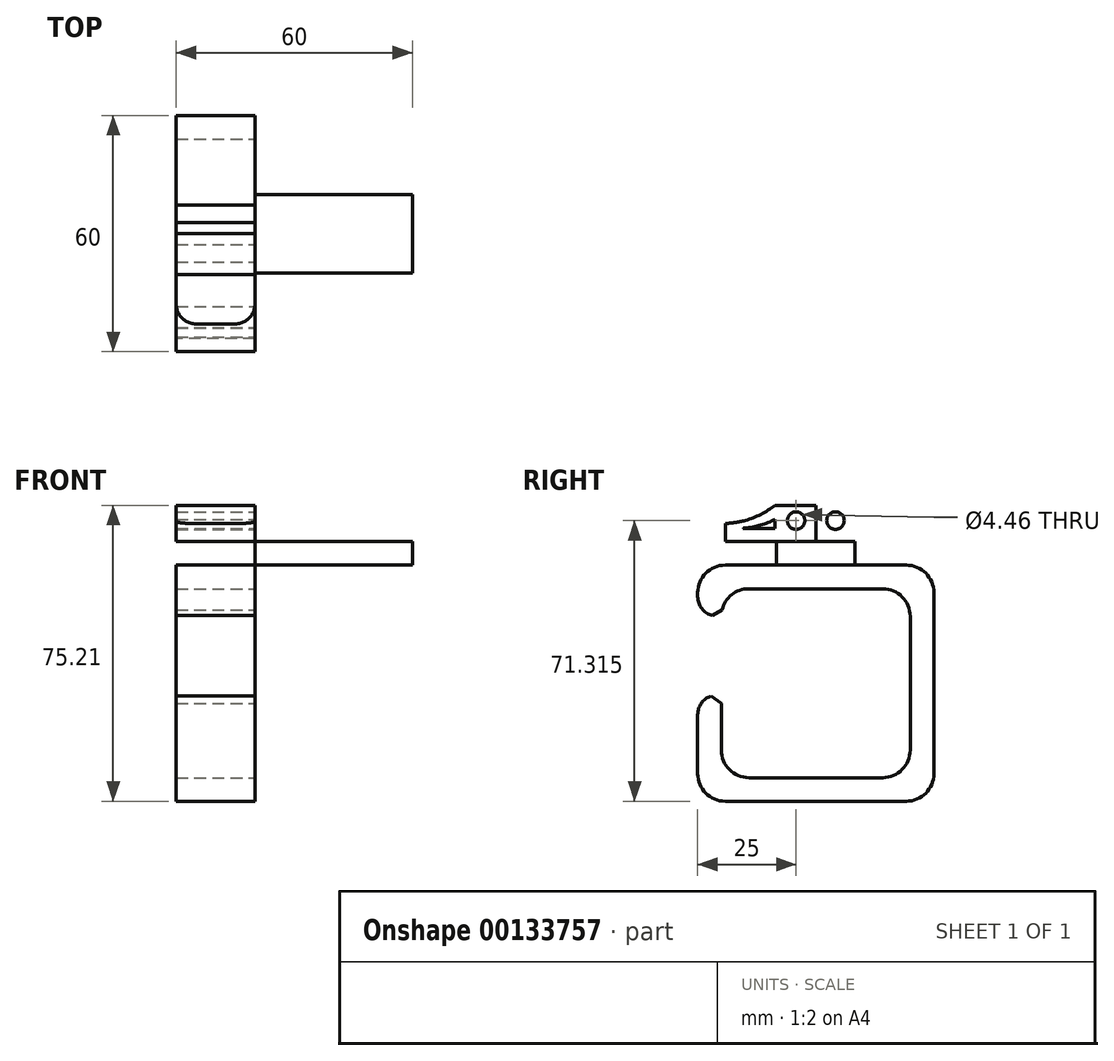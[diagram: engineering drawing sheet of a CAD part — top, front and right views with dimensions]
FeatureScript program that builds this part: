
annotation { "Feature Type Name" : "Feature", "Feature Type Description" : "" }
export const myFeature = defineFeature(function(context is Context, id is Id, definition is map)
    precondition{}
    {
        {
            var Q0;
            Q0=qCreatedBy(makeId("Right.planeOp"),FACE);
            var sketch = newSketch(context, id + "F0", { "sketchPlane" : qUnion([Q0])});
            skLineSegment(sketch, "E0", {"start": v(0, 0) * mm, "end": v(48.5, 0) * mm});
            skLineSegment(sketch, "E1", {"start": v(48.5, 0) * mm, "end": v(48.5, 25) * mm});
            skLineSegment(sketch, "E2", {"start": v(48.5, 25) * mm, "end": v(-71.5, 25) * mm});
            skLineSegment(sketch, "E3", {"start": v(-71.5, 25) * mm, "end": v(-71.5, 0) * mm});
            skLineSegment(sketch, "E4", {"start": v(-71.5, 0) * mm, "end": v(-23, 0) * mm});
            skLineSegment(sketch, "E5", {"start": v(-40, 0) * mm, "end": v(-40, 25) * mm});
            skLineSegment(sketch, "E6", {"start": v(17, 0) * mm, "end": v(17, 25) * mm});
            skLineSegment(sketch, "E7.0", {"start": v(-68.5, 3) * mm, "end": v(-23, 3) * mm});
            skLineSegment(sketch, "E7.1", {"start": v(0, 3) * mm, "end": v(45.5, 3) * mm});
            skLineSegment(sketch, "E7.2", {"start": v(45.5, 3) * mm, "end": v(45.5, 22) * mm});
            skLineSegment(sketch, "E7.3", {"start": v(45.5, 22) * mm, "end": v(-68.5, 22) * mm});
            skLineSegment(sketch, "E7.4", {"start": v(-68.5, 22) * mm, "end": v(-68.5, 3) * mm});
            skLineSegment(sketch, "E8", {"start": v(-23, 3) * mm, "end": v(-23, 0) * mm});
            skLineSegment(sketch, "E9", {"start": v(0, 3) * mm, "end": v(0, 0) * mm});
            skSolve(sketch);
        }
        {
            var Q0;
            {var subQ0=sQuery(id+"F0.wireOp",EDGE,"E8");Q0=makeQuery(id+"F0.imprint","IMPRINT",FACE,{"disambiguationData":[TD([[makeQuery(id+"F0.imprint","IMPRINT",EDGE,{"derivedFrom":subQ0}),-1.0]])]});}
            var Q1;
            {var subQ8=sQuery(id+"F0.wireOp",EDGE,"E3");Q1=makeQuery(id+"F0.imprint","IMPRINT",FACE,{"disambiguationData":[TD([[makeQuery(id+"F0.imprint","IMPRINT",EDGE,{"derivedFrom":subQ8}),1.0]])]});}
            var Q2;
            {var subQ0=sQuery(id+"F0.wireOp",EDGE,"E5");var subQ1=sQuery(id+"F0.wireOp",EDGE,"E2");var subQ2=makeQuery(id+"F0.imprint","INTERSECT",VERTEX,{"derivedFrom":[subQ1,subQ0]});Q2=makeQuery(id+"F0.imprint","IMPRINT",FACE,{"disambiguationData":[TD([[makeQuery(id+"F0.imprint","IMPRINT",EDGE,{"disambiguationData":[TD([[subQ2,1.0]])],"derivedFrom":subQ1}),1.0]])]});}
            var Q3;
            {var subQ6=sQuery(id+"F0.wireOp",EDGE,"E1");Q3=makeQuery(id+"F0.imprint","IMPRINT",FACE,{"disambiguationData":[TD([[makeQuery(id+"F0.imprint","IMPRINT",EDGE,{"derivedFrom":subQ6}),1.0]])]});}
            var Q4;
            {var subQ0=sQuery(id+"F0.wireOp",EDGE,"E9");Q4=makeQuery(id+"F0.imprint","IMPRINT",FACE,{"disambiguationData":[TD([[makeQuery(id+"F0.imprint","IMPRINT",EDGE,{"derivedFrom":subQ0}),1.0]])]});}
            var Q5;
            {var subQ5=sQuery(id+"F0.wireOp",EDGE,"E7.2");Q5=makeQuery(id+"F0.imprint","IMPRINT",FACE,{"disambiguationData":[TD([[makeQuery(id+"F0.imprint","IMPRINT",EDGE,{"derivedFrom":subQ5}),1.0]])]});}
            var Q6;
            {var subQ5=sQuery(id+"F0.wireOp",EDGE,"E7.4");Q6=makeQuery(id+"F0.imprint","IMPRINT",FACE,{"disambiguationData":[TD([[makeQuery(id+"F0.imprint","IMPRINT",EDGE,{"derivedFrom":subQ5}),1.0]])]});}
            extrude(context, id + "F1", {"entities" : qUnion([Q0, Q1, Q2, Q3, Q4, Q5, Q6]), "depth" : 100 * mm});
        }
        {
            var Q0;
            Q0=makeQuery(id+"F1.opExtrude","CAP_FACE",FACE,{"disambiguationData":[OSD([sQuery(id+"F0.wireOp",EDGE,"E0"),sQuery(id+"F0.wireOp",EDGE,"E1"),sQuery(id+"F0.wireOp",EDGE,"E2"),sQuery(id+"F0.wireOp",EDGE,"E3"),sQuery(id+"F0.wireOp",EDGE,"E4"),sQuery(id+"F0.wireOp",EDGE,"E5"),sQuery(id+"F0.wireOp",EDGE,"E6"),sQuery(id+"F0.wireOp",EDGE,"E7.0"),sQuery(id+"F0.wireOp",EDGE,"E7.1"),sQuery(id+"F0.wireOp",EDGE,"E7.3"),sQuery(id+"F0.wireOp",EDGE,"E8"),sQuery(id+"F0.wireOp",EDGE,"E9")])],"isStart":false});
            var sketch = newSketch(context, id + "F2", { "sketchPlane" : qUnion([Q0])});
            skLineSegment(sketch, "E10.bottom", {"start": v(-34.5, -2.96) * mm, "end": v(11.5, -2.96) * mm});
            skLineSegment(sketch, "E11", {"start": v(-11.5, 25) * mm, "end": v(-11.5, -62.96) * mm, "construction": true});
            skCircle(sketch, "E12", {"center": v(-16.5, 8.36) * mm, "radius": 2.23 * mm});
            skCircle(sketch, "E13.MirrorC", {"center": v(-6.5, 8.36) * mm, "radius": 2.23 * mm});
            skArc(sketch, "E14", {"start": v(-30.06, 6.4) * mm, "mid": v(-25.83, 7.13) * mm, "end": v(-21.84, 8.68) * mm});
            skLineSegment(sketch, "E15", {"start": v(-30.06, 6.4) * mm, "end": v(-21.84, 6.4) * mm});
            skLineSegment(sketch, "E16", {"start": v(-21.84, 6.4) * mm, "end": v(-21.84, 8.68) * mm});
            skLineSegment(sketch, "E17.MirrorCS", {"start": v(7.06, 6.4) * mm, "end": v(-1.16, 6.4) * mm});
            skLineSegment(sketch, "E18.MirrorCS", {"start": v(-1.16, 6.4) * mm, "end": v(-1.16, 8.68) * mm});
            skArc(sketch, "E19.MirrorCS", {"start": v(7.06, 6.4) * mm, "mid": v(2.83, 7.13) * mm, "end": v(-1.16, 8.68) * mm});
            skLineSegment(sketch, "E20.top", {"start": v(-21.5, -62.96) * mm, "end": v(-1.5, -62.96) * mm, "construction": true});
            skLineSegment(sketch, "E21.bottom", {"start": v(-34.5, -62.96) * mm, "end": v(11.5, -62.96) * mm});
            skLineSegment(sketch, "E21.left", {"start": v(-41.5, -55.96) * mm, "end": v(-41.5, -9.96) * mm});
            skLineSegment(sketch, "E21.right", {"start": v(18.5, -55.96) * mm, "end": v(18.5, -9.96) * mm});
            skPoint(sketch, "E22.orphan", {"position": v(-11.5, -18.14) * mm});
            skLineSegment(sketch, "E23.bottom", {"start": v(-21.5, -2.96) * mm, "end": v(-1.5, -2.96) * mm});
            skLineSegment(sketch, "E23.top", {"start": v(-21.5, -2.96) * mm, "end": v(-1.5, -2.96) * mm});
            skLineSegment(sketch, "E23.left", {"start": v(-21.5, -2.96) * mm, "end": v(-21.5, -2.96) * mm});
            skLineSegment(sketch, "E23.right", {"start": v(-1.5, -2.96) * mm, "end": v(-1.5, -2.96) * mm});
            skLineSegment(sketch, "E24.0", {"start": v(-28.5, -8.96) * mm, "end": v(5.5, -8.96) * mm});
            skLineSegment(sketch, "E24.1", {"start": v(-35.5, -49.96) * mm, "end": v(-35.5, -15.96) * mm});
            skLineSegment(sketch, "E24.2", {"start": v(-28.5, -56.96) * mm, "end": v(5.5, -56.96) * mm});
            skLineSegment(sketch, "E24.3", {"start": v(12.5, -49.96) * mm, "end": v(12.5, -15.96) * mm});
            skPoint(sketch, "E25.visualSharp", {"position": v(-41.5, -2.96) * mm});
            skArc(sketch, "E25.filletArc", {"start": v(-34.5, -2.96) * mm, "mid": v(-39.45, -5) * mm, "end": v(-41.5, -9.96) * mm});
            skPoint(sketch, "E26.visualSharp", {"position": v(18.5, -2.96) * mm});
            skArc(sketch, "E26.filletArc", {"start": v(18.5, -9.96) * mm, "mid": v(16.45, -5) * mm, "end": v(11.5, -2.96) * mm});
            skPoint(sketch, "E27.visualSharp", {"position": v(18.5, -62.96) * mm});
            skArc(sketch, "E27.filletArc", {"start": v(11.5, -62.96) * mm, "mid": v(16.45, -60.9) * mm, "end": v(18.5, -55.96) * mm});
            skPoint(sketch, "E28.visualSharp", {"position": v(-41.5, -62.96) * mm});
            skArc(sketch, "E28.filletArc", {"start": v(-41.5, -55.96) * mm, "mid": v(-39.45, -60.9) * mm, "end": v(-34.5, -62.96) * mm});
            skPoint(sketch, "E29.visualSharp", {"position": v(-35.5, -8.96) * mm});
            skArc(sketch, "E29.filletArc", {"start": v(-28.5, -8.96) * mm, "mid": v(-33.45, -11) * mm, "end": v(-35.5, -15.96) * mm});
            skPoint(sketch, "E30.visualSharp", {"position": v(12.5, -8.96) * mm});
            skArc(sketch, "E30.filletArc", {"start": v(12.5, -15.96) * mm, "mid": v(10.45, -11) * mm, "end": v(5.5, -8.96) * mm});
            skPoint(sketch, "E31.visualSharp", {"position": v(12.5, -56.96) * mm});
            skArc(sketch, "E31.filletArc", {"start": v(5.5, -56.96) * mm, "mid": v(10.45, -54.9) * mm, "end": v(12.5, -49.96) * mm});
            skPoint(sketch, "E32.visualSharp", {"position": v(-35.5, -56.96) * mm});
            skArc(sketch, "E32.filletArc", {"start": v(-35.5, -49.96) * mm, "mid": v(-33.45, -54.9) * mm, "end": v(-28.5, -56.96) * mm});
            skLineSegment(sketch, "E33.bottom", {"start": v(-35.5, -15.96) * mm, "end": v(-41.5, -15.96) * mm});
            skLineSegment(sketch, "E33.top", {"start": v(-35.5, -35.96) * mm, "end": v(-41.5, -35.96) * mm});
            skLineSegment(sketch, "E33.left", {"start": v(-35.5, -15.96) * mm, "end": v(-35.5, -35.96) * mm});
            skLineSegment(sketch, "E33.right", {"start": v(-41.5, -15.96) * mm, "end": v(-41.5, -35.96) * mm});
            skLineSegment(sketch, "E34.bottom", {"start": v(-11.5, 3.04) * mm, "end": v(-34.42, 3.04) * mm});
            skLineSegment(sketch, "E34.top", {"start": v(-11.5, 12.25) * mm, "end": v(-21.88, 12.25) * mm});
            skLineSegment(sketch, "E34.left", {"start": v(-11.5, 3.04) * mm, "end": v(-11.5, 12.25) * mm});
            skLineSegment(sketch, "E34.right", {"start": v(-34.42, 3.04) * mm, "end": v(-34.42, 7.65) * mm});
            skLineSegment(sketch, "E35.MirrorCS", {"start": v(-11.5, 12.25) * mm, "end": v(-1.12, 12.25) * mm});
            skLineSegment(sketch, "E36.MirrorCS", {"start": v(11.42, 3.04) * mm, "end": v(11.42, 7.65) * mm});
            skLineSegment(sketch, "E37.MirrorCS", {"start": v(-11.5, 3.04) * mm, "end": v(11.42, 3.04) * mm});
            skArc(sketch, "E38", {"start": v(-34.42, 7.65) * mm, "mid": v(-27.78, 8.93) * mm, "end": v(-21.88, 12.25) * mm});
            skArc(sketch, "E39.MirrorCS", {"start": v(11.42, 7.65) * mm, "mid": v(4.78, 8.93) * mm, "end": v(-1.12, 12.25) * mm});
            skPoint(sketch, "E40.orphan", {"position": v(-34.42, 12.25) * mm});
            skPoint(sketch, "E41.orphan", {"position": v(11.42, 12.25) * mm});
            skLineSegment(sketch, "E42.top", {"start": v(-21.5, 3.04) * mm, "end": v(-1.5, 3.04) * mm});
            skLineSegment(sketch, "E42.left", {"start": v(-21.5, -2.96) * mm, "end": v(-21.5, 3.04) * mm});
            skLineSegment(sketch, "E42.right", {"start": v(-1.5, -2.96) * mm, "end": v(-1.5, 3.04) * mm});
            skSolve(sketch);
        }
        {
            var Q0;
            Q0=makeQuery(id+"F2.imprint","IMPRINT",FACE,{"disambiguationData":[TD([[makeQuery(id+"F2.imprint","IMPRINT",EDGE,{"derivedFrom":sQuery(id+"F2.wireOp",EDGE,"E10.bottom")}),1.0]])]});
            extrude(context, id + "F3", {"entities" : qUnion([Q0]), "depth" : 40 * mm});
        }
        {
            var Q0;
            Q0=makeQuery(id+"F2.imprint","IMPRINT",FACE,{"disambiguationData":[TD([[makeQuery(id+"F2.imprint","IMPRINT",EDGE,{"derivedFrom":sQuery(id+"F2.wireOp",EDGE,"E12")}),-1.0]])]});
            var Q1;
            Q1=makeQuery(id+"F2.imprint","IMPRINT",FACE,{"disambiguationData":[TD([[makeQuery(id+"F2.imprint","IMPRINT",EDGE,{"derivedFrom":sQuery(id+"F2.wireOp",EDGE,"E13.MirrorC")}),1.0]])]});
            var Q2;
            Q2=makeQuery(id+"F2.imprint","IMPRINT",FACE,{"disambiguationData":[TD([[makeQuery(id+"F2.imprint","IMPRINT",EDGE,{"derivedFrom":sQuery(id+"F2.wireOp",EDGE,"E23.bottom")}),1.0]])]});
            var Q3;
            Q3=makeQuery(id+"F2.imprint","IMPRINT",FACE,{"disambiguationData":[TD([[makeQuery(id+"F2.imprint","IMPRINT",EDGE,{"derivedFrom":sQuery(id+"F2.wireOp",EDGE,"E21.bottom")}),1.0]])]});
            extrude(context, id + "F4", {"entities" : qUnion([Q0, Q1, Q2, Q3]), "oppositeDirection" : true, "depth" : 20 * mm});
        }
        {
            var Q0;
            Q0=makeQuery(id+"F4.opExtrude","CAP_EDGE",EDGE,{"disambiguationData":[OSD([sQuery(id+"F2.wireOp",EDGE,"E34.right")])],"isStart":true});
            var Q1;
            Q1=makeQuery(id+"F4.opExtrude","CAP_EDGE",EDGE,{"disambiguationData":[OSD([sQuery(id+"F2.wireOp",EDGE,"E36.MirrorCS")])],"isStart":true});
            var Q2;
            Q2=makeQuery(id+"F4.opExtrude","CAP_EDGE",EDGE,{"disambiguationData":[OSD([sQuery(id+"F2.wireOp",EDGE,"E42.right")])],"isStart":true});
            var Q3;
            Q3=makeQuery(id+"F4.opExtrude","CAP_EDGE",EDGE,{"disambiguationData":[OSD([sQuery(id+"F2.wireOp",EDGE,"E42.left")])],"isStart":true});
            var Q4;
            Q4=makeQuery(id+"F4.opExtrude","CAP_EDGE",EDGE,{"disambiguationData":[OSD([sQuery(id+"F2.wireOp",EDGE,"E42.left")])],"isStart":false});
            var Q5;
            Q5=makeQuery(id+"F4.opExtrude","CAP_EDGE",EDGE,{"disambiguationData":[OSD([sQuery(id+"F2.wireOp",EDGE,"E42.right")])],"isStart":false});
            var Q6;
            Q6=makeQuery(id+"F4.opExtrude","CAP_EDGE",EDGE,{"disambiguationData":[OSD([sQuery(id+"F2.wireOp",EDGE,"E34.right")])],"isStart":false});
            var Q7;
            Q7=makeQuery(id+"F4.opExtrude","CAP_EDGE",EDGE,{"disambiguationData":[OSD([sQuery(id+"F2.wireOp",EDGE,"E36.MirrorCS")])],"isStart":false});
            fillet(context, id + "F5", {"entities" : qUnion([Q0, Q1, Q2, Q3, Q4, Q5, Q6, Q7]), "radius" : 5 * mm, "tangentPropagation" : true, "allowEdgeOverflow" : false});
        }
        {
            var Q0;
            Q0=makeQuery(id+"F4.opExtrude","SWEPT_EDGE",EDGE,{"disambiguationData":[OSD([sQuery(id+"F2.wireOp",EDGE,"E21.left"),sQuery(id+"F2.wireOp",EDGE,"E33.bottom"),sQuery(id+"F2.wireOp",EDGE,"E33.right")])]});
            var Q1;
            Q1=makeQuery(id+"F4.opExtrude","SWEPT_EDGE",EDGE,{"disambiguationData":[OSD([sQuery(id+"F2.wireOp",EDGE,"E21.left"),sQuery(id+"F2.wireOp",EDGE,"E33.top"),sQuery(id+"F2.wireOp",EDGE,"E33.right")])]});
            fillet(context, id + "F6", {"entities" : qUnion([Q0, Q1]), "radius" : 5 * mm, "tangentPropagation" : true, "allowEdgeOverflow" : false});
        }
        {
            var Q0;
            Q0=makeQuery(id+"F4.opExtrude","SWEPT_EDGE",EDGE,{"disambiguationData":[OSD([sQuery(id+"F2.wireOp",EDGE,"E29.filletArc"),sQuery(id+"F2.wireOp",EDGE,"E33.bottom"),sQuery(id+"F2.wireOp",EDGE,"E33.left")])]});
            var Q1;
            Q1=makeQuery(id+"F4.opExtrude","SWEPT_EDGE",EDGE,{"disambiguationData":[OSD([sQuery(id+"F2.wireOp",EDGE,"E24.1"),sQuery(id+"F2.wireOp",EDGE,"E33.top"),sQuery(id+"F2.wireOp",EDGE,"E33.left")])]});
            chamfer(context, id + "F7", {"entities" : qUnion([Q0, Q1]), "width" : 2 * mm, "tangentPropagation" : true});
        }
        {
            var Q0;
            Q0=makeQuery(id+"F1.opExtrude","SWEPT_BODY",BODY,{"disambiguationData":[OSD([sQuery(id+"F0.wireOp",EDGE,"E0"),sQuery(id+"F0.wireOp",EDGE,"E1"),sQuery(id+"F0.wireOp",EDGE,"E2"),sQuery(id+"F0.wireOp",EDGE,"E3"),sQuery(id+"F0.wireOp",EDGE,"E4"),sQuery(id+"F0.wireOp",EDGE,"E5"),sQuery(id+"F0.wireOp",EDGE,"E6"),sQuery(id+"F0.wireOp",EDGE,"E7.0"),sQuery(id+"F0.wireOp",EDGE,"E7.1"),sQuery(id+"F0.wireOp",EDGE,"E7.3"),sQuery(id+"F0.wireOp",EDGE,"E8"),sQuery(id+"F0.wireOp",EDGE,"E9")])]});
            deleteBodies(context, id + "F8", {"entities" : qUnion([Q0])});
        }
    });
